# Revit family: Pet_Fountain-Wall_Mounted-Murdock_Manufacturing-GRT_Series
name_source: partatom
category: Plumbing Fixtures
units: mm (PartAtom-declared; Revit-internal decimal feet)

## family parameters
Cut with Voids When Loaded = No
Host = Face
OmniClass Number = 23.65.70.14.11
OmniClass Title = Drinking Fountains/Coolers
Part Type = Normal
Room Calculation Point = No
Round Connector Dimension = Use Diameter
Shared = Yes

## types (4) — shared parameters
-FRU1 - Underground Freeze-Resistant Valve for One Pushbutton = No
-NP1 - Non-pollutable, freeze resistant valve = No
-RFS - Round Free Standing Bowl = No
Assembly Code = D2010810
Bubbler Material = Stainless Steel-Murdock-Polished
CW Connection = Yes
CWFU = 1.5
Compliance Certifications = Unit shall be certified to Public Law 111-380 (NO-LEAD) and NSF/ANSI/CAN 61.
Default Elevation = 34"
Description = Round Stainless Steel Pet Fountain
HW Connection = No
HWFU = 1.5
Height = 7 5/8"
Inlet Connection Diameter = 1/2"
Inlet Connection Height = 4"
Installation Type = Wall Mounted
Length = 13"
Manufacturer = Murdock Manufacturing
Outlet Connection Height = 2"
Pressure Range = 20-105 psig.
Product Documentation Link = https://www.murdockmfg.com
Product Page URL = https://www.murdockmfg.com
URL = http://www.murdockmfg.com
Vent Connection = No
WFU = 2
Waste Connection = Yes
Waste Connection Diameter = 1 1/4"
Width = 12 1/2"

## per-type parameters (varying)
| type | Body Material | Material | Type Comments |
| GRT75-PF | Stainless Steel-Murdock-Powder Coated Green | Stainless Steel-Murdock-Powder Coated Green | Green powder-coated |
| GRT74-PF | Stainless Steel-Murdock-Satin | Stainless Steel-Murdock-Satin | Satin stainless finish |
| GRT76-PF | Stainless Steel-Murdock-Powder Coated Red | Stainless Steel-Murdock-Powder Coated Red | Red powder-coated |
| GRT77-PF | Stainless Steel-Murdock-Powder Coated Blue | Stainless Steel-Murdock-Powder Coated Blue | Blue powder-coated |

note: column(s) folded — value = type name in every type: Model

## geometry (parser evidence)
native form markers: Sweep x3
no freeform markers — native parametric forms only
